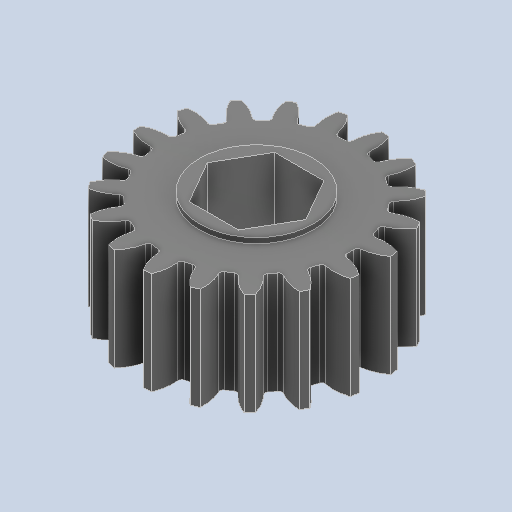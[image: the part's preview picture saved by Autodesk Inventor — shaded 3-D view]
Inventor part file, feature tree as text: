
AUTODESK INVENTOR PART (.ipt)
format: ipt  version: 2024.2 (Build 282272000, 272)  size: 250,880 bytes
history: native  units: in
note: dims shown in document units (in); Inventor stores cm internally (conversion verified against a paired STEP export)
features: fillet x1
ambient origin geometry x8: Origin, YZ Plane, XZ Plane, XY Plane, X Axis, Y Axis, Z Axis, Center Point
bodies: Solid1 (feature_tree)
feature tree (1):
  fillet  "Fillet1"  [1 undecoded]
note: 1 required parameter value undecoded (feature->parameter linkage not recoverable at this tier; creation-order binding heuristic only, values carry confidence <= 0.55)
